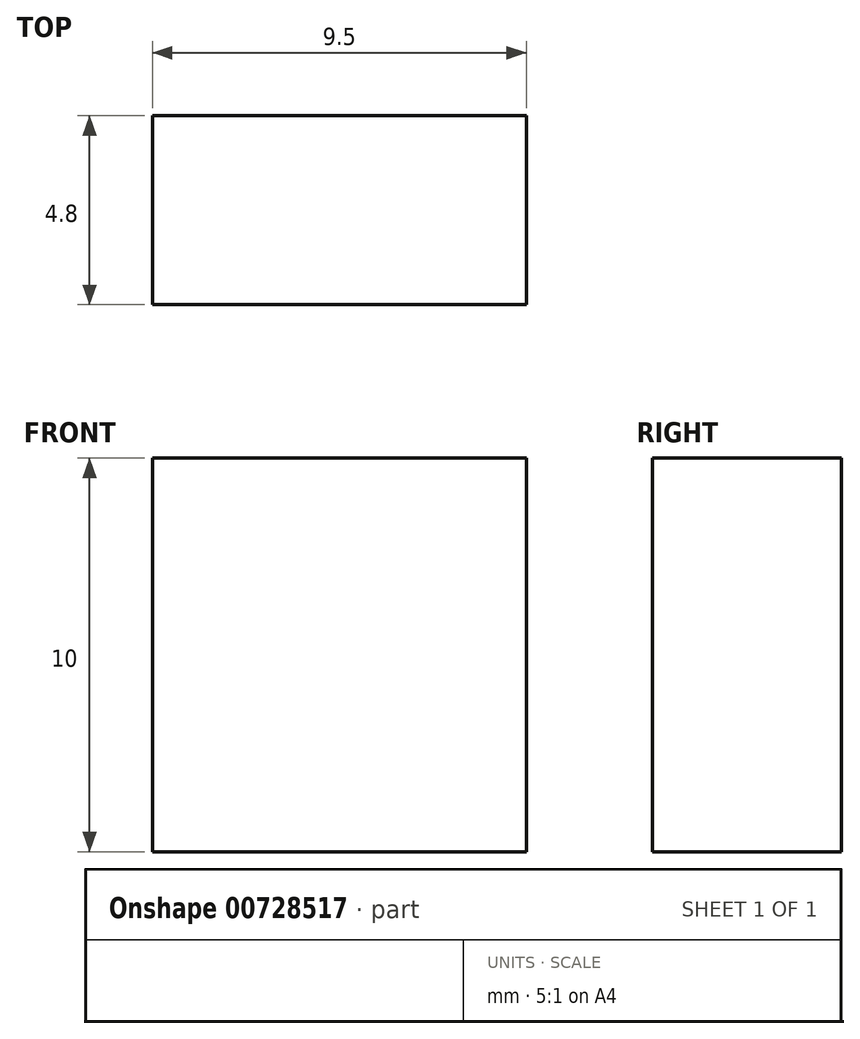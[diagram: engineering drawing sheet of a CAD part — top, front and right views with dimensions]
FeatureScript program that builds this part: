
annotation { "Feature Type Name" : "Feature", "Feature Type Description" : "" }
export const myFeature = defineFeature(function(context is Context, id is Id, definition is map)
    precondition{}
    {
        {
            var Q0;
            Q0=qCreatedBy(makeId("Top.planeOp"),FACE);
            var sketch = newSketch(context, id + "F0", { "sketchPlane" : qUnion([Q0])});
            skLineSegment(sketch, "E0.bottom", {"start": v(-9.5, 0) * mm, "end": v(0, 0) * mm});
            skLineSegment(sketch, "E0.top", {"start": v(-9.5, 4.8) * mm, "end": v(0, 4.8) * mm});
            skLineSegment(sketch, "E0.left", {"start": v(-9.5, 0) * mm, "end": v(-9.5, 4.8) * mm});
            skLineSegment(sketch, "E0.right", {"start": v(0, 0) * mm, "end": v(0, 4.8) * mm});
            skSolve(sketch);
        }
        {
            var Q0;
            Q0 = qSketchRegion(id + "FRaLAdPDH5cZm7y_1", true);
            var Q1;
            Q1 = qSketchRegion(id + "F0", true);
            extrude(context, id + "F1", {"entities" : qUnion([Q0, Q1]), "depth" : 10 * mm, "offsetDistance" : 25 * mm});
        }
    });
